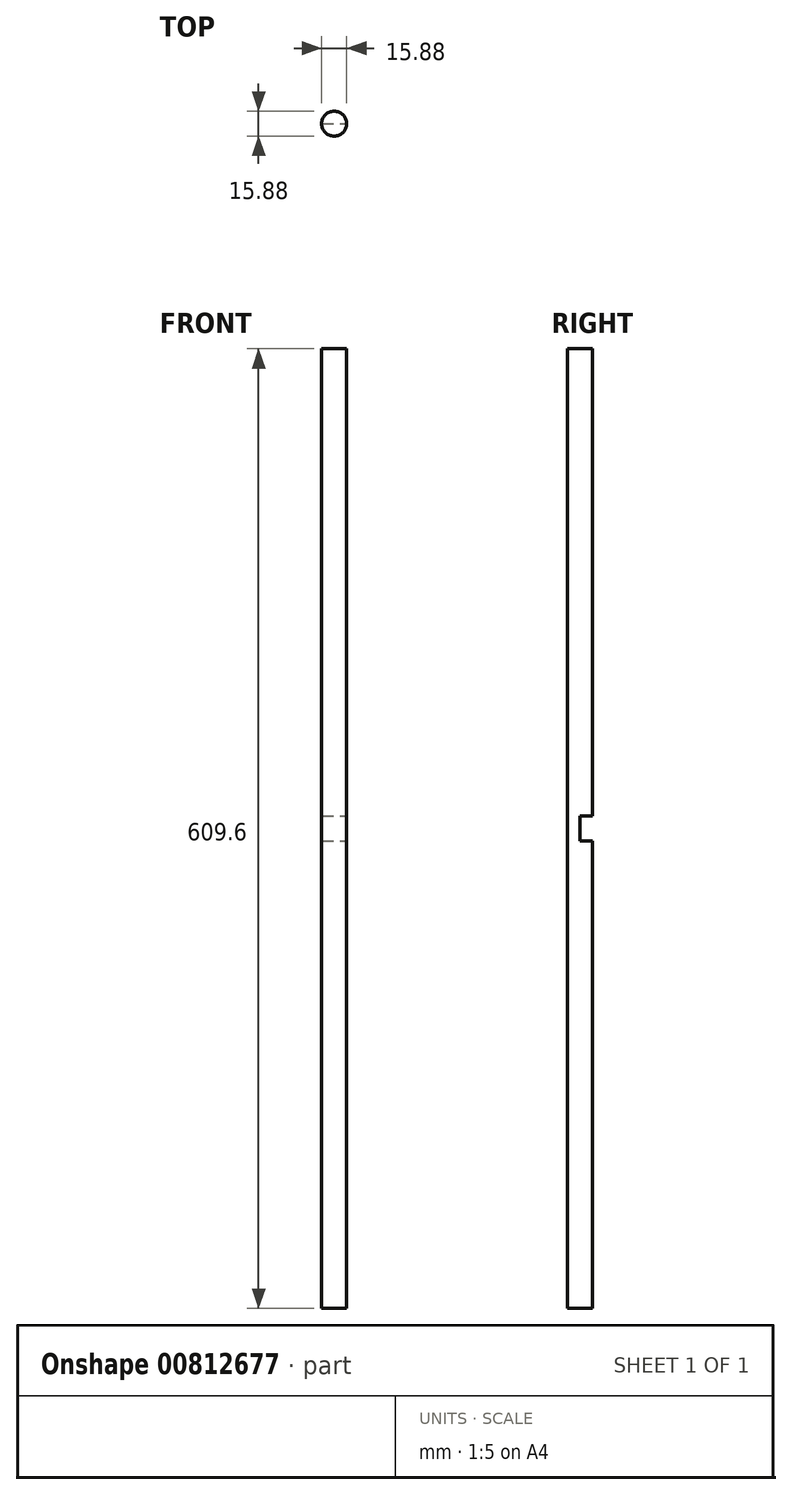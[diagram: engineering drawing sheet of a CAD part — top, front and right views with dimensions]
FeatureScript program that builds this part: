
annotation { "Feature Type Name" : "Feature", "Feature Type Description" : "" }
export const myFeature = defineFeature(function(context is Context, id is Id, definition is map)
    precondition{}
    {
        {
            var Q0;
            Q0=qCreatedBy(makeId("Top.planeOp"),FACE);
            var sketch = newSketch(context, id + "F0", { "sketchPlane" : qUnion([Q0])});
            skCircle(sketch, "E0", {"center": v(0, 0) * mm, "radius": 7.94 * mm});
            skSolve(sketch);
        }
        {
            var Q0;
            Q0 = qSketchRegion(id + "F0", true);
            extrude(context, id + "F1", {"entities" : qUnion([Q0]), "endBound" : BoundingType.SYMMETRIC, "depth" : 609.6 * mm, "offsetDistance" : 25.4 * mm});
        }
        {
            var Q0;
            Q0=qCreatedBy(makeId("Right.planeOp"),FACE);
            var sketch = newSketch(context, id + "F2", { "sketchPlane" : qUnion([Q0])});
            skLineSegment(sketch, "E1.bottom", {"start": v(0, 7.94) * mm, "end": v(7.94, 7.94) * mm});
            skLineSegment(sketch, "E1.top", {"start": v(0, -7.94) * mm, "end": v(7.94, -7.94) * mm});
            skLineSegment(sketch, "E1.left", {"start": v(0, 7.94) * mm, "end": v(0, -7.94) * mm});
            skLineSegment(sketch, "E1.right", {"start": v(7.94, 7.94) * mm, "end": v(7.94, -7.94) * mm});
            skSolve(sketch);
        }
        {
            var Q0;
            Q0 = qSketchRegion(id + "F2", true);
            extrude(context, id + "F3", {"entities" : qUnion([Q0]), "operationType" : NewBodyOperationType.REMOVE, "endBound" : BoundingType.SYMMETRIC, "oppositeDirection" : true, "depth" : 25.4 * mm, "offsetDistance" : 25.4 * mm});
        }
    });
